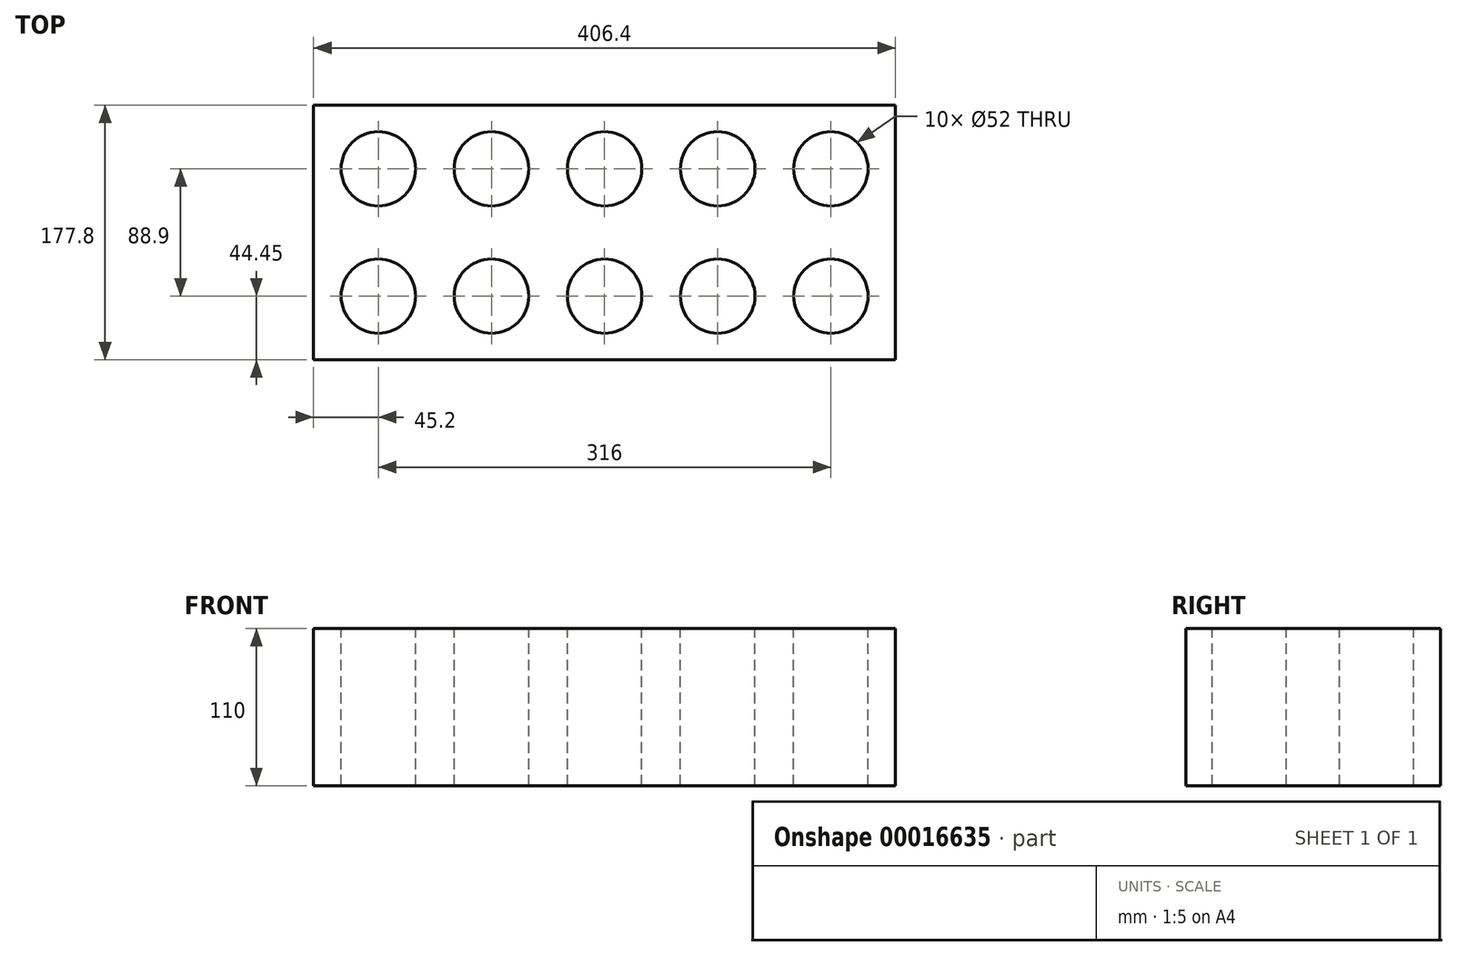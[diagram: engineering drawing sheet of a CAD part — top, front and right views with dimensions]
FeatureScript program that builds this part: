
annotation { "Feature Type Name" : "Feature", "Feature Type Description" : "" }
export const myFeature = defineFeature(function(context is Context, id is Id, definition is map)
    precondition{}
    {
        {
            var Q0;
            Q0=qCreatedBy(makeId("Top.planeOp"),FACE);
            var sketch = newSketch(context, id + "F0", { "sketchPlane" : qUnion([Q0])});
            skLineSegment(sketch, "E0.bottom", {"start": v(0, 0) * mm, "end": v(406.4, 0) * mm});
            skLineSegment(sketch, "E0.top", {"start": v(0, 177.8) * mm, "end": v(406.4, 177.8) * mm});
            skLineSegment(sketch, "E0.left", {"start": v(0, 0) * mm, "end": v(0, 177.8) * mm});
            skLineSegment(sketch, "E0.right", {"start": v(406.4, 0) * mm, "end": v(406.4, 177.8) * mm});
            skSolve(sketch);
        }
        {
            var Q0;
            Q0=makeQuery(id+"F0.imprint","IMPRINT",FACE,{"disambiguationData":[TD([[makeQuery(id+"F0.imprint","IMPRINT",EDGE,{"derivedFrom":sQuery(id+"F0.wireOp",EDGE,"E0.bottom")}),1.0]])]});
            extrude(context, id + "F1", {"entities" : qUnion([Q0]), "depth" : 110 * mm, "offsetDistance" : 25 * mm});
        }
        {
            var Q0;
            Q0=makeQuery(id+"F1.opExtrude","CAP_FACE",FACE,{"disambiguationData":[OSD([sQuery(id+"F0.wireOp",EDGE,"E0.bottom"),sQuery(id+"F0.wireOp",EDGE,"E0.top"),sQuery(id+"F0.wireOp",EDGE,"E0.left"),sQuery(id+"F0.wireOp",EDGE,"E0.right")])],"isStart":false});
            var sketch = newSketch(context, id + "F2", { "sketchPlane" : qUnion([Q0])});
            skCircle(sketch, "E1", {"center": v(203.2, 133.35) * mm, "radius": 26 * mm});
            skLineSegment(sketch, "E2", {"start": v(0, 88.9) * mm, "end": v(406.4, 88.9) * mm, "construction": true});
            skLineSegment(sketch, "E3", {"start": v(203.2, 177.8) * mm, "end": v(203.2, 0) * mm, "construction": true});
            skCircle(sketch, "E4", {"center": v(203.2, 44.45) * mm, "radius": 26 * mm});
            skCircle(sketch, "E5.1.0.0", {"center": v(282.2, 133.35) * mm, "radius": 26 * mm});
            skCircle(sketch, "E5.1.0.1", {"center": v(282.2, 44.45) * mm, "radius": 26 * mm});
            skCircle(sketch, "E5.2.0.0", {"center": v(361.2, 133.35) * mm, "radius": 26 * mm});
            skCircle(sketch, "E5.2.0.1", {"center": v(361.2, 44.45) * mm, "radius": 26 * mm});
            skLineSegment(sketch, "E5.direction1", {"start": v(203.2, 133.35) * mm, "end": v(282.2, 133.35) * mm, "construction": true});
            skCircle(sketch, "E6.1.0.0", {"center": v(124.2, 133.35) * mm, "radius": 26 * mm});
            skCircle(sketch, "E6.1.0.1", {"center": v(124.2, 44.45) * mm, "radius": 26 * mm});
            skCircle(sketch, "E6.2.0.0", {"center": v(45.2, 133.35) * mm, "radius": 26 * mm});
            skCircle(sketch, "E6.2.0.1", {"center": v(45.2, 44.45) * mm, "radius": 26 * mm});
            skLineSegment(sketch, "E6.direction1", {"start": v(203.2, 44.45) * mm, "end": v(124.2, 44.45) * mm, "construction": true});
            skSolve(sketch);
        }
        {
            var Q0;
            Q0 = qSketchRegion(id + "F2", true);
            extrude(context, id + "F3", {"entities" : qUnion([Q0]), "operationType" : NewBodyOperationType.REMOVE, "endBound" : BoundingType.THROUGH_ALL, "oppositeDirection" : true, "depth" : 25 * mm, "offsetDistance" : 25 * mm});
        }
    });
